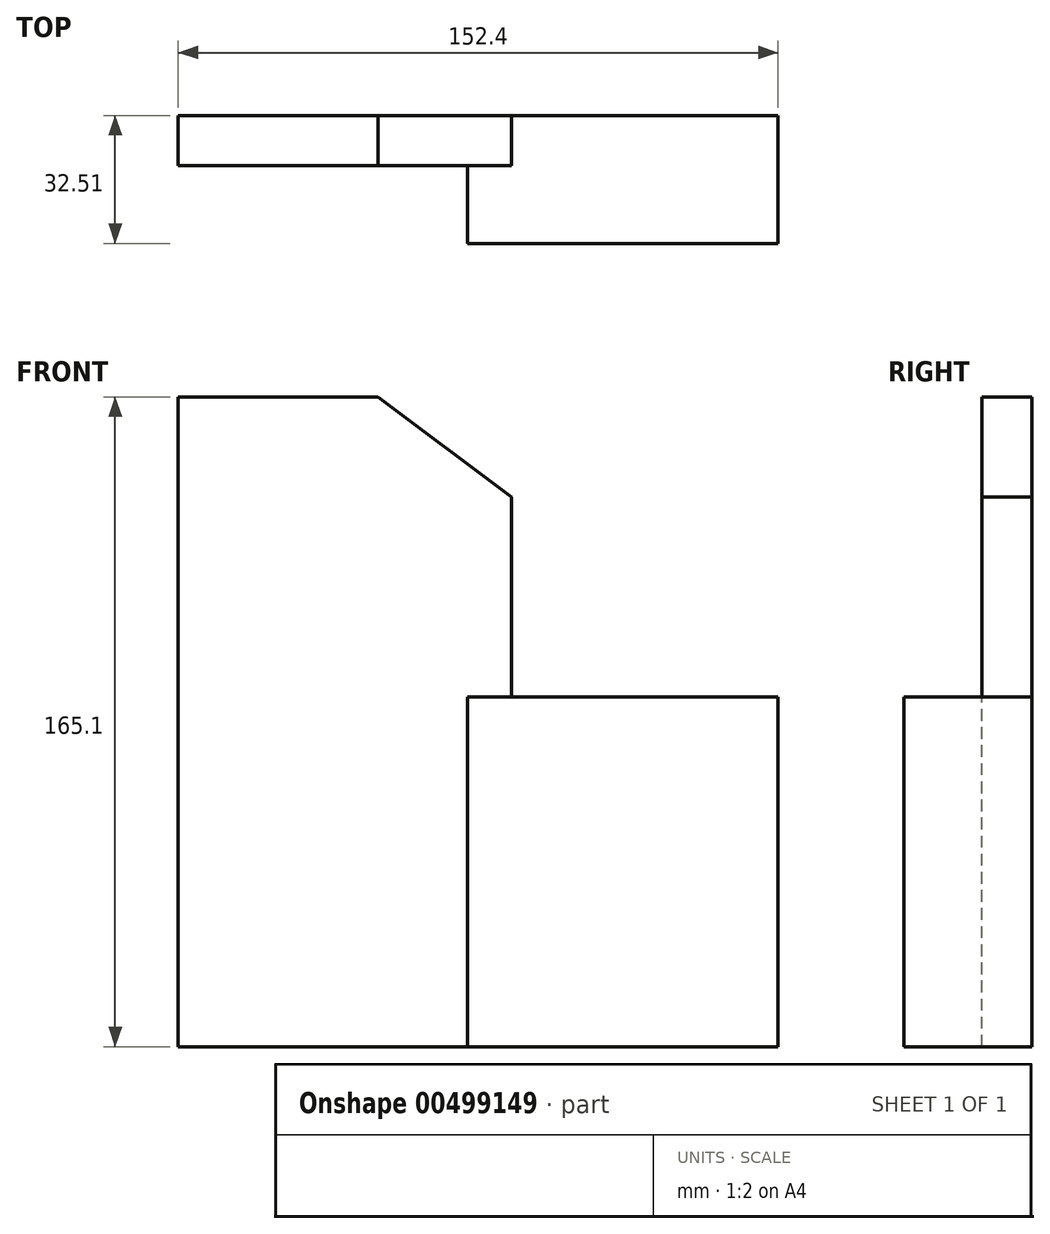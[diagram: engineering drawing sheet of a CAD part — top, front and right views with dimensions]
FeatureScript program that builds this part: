
annotation { "Feature Type Name" : "Feature", "Feature Type Description" : "" }
export const myFeature = defineFeature(function(context is Context, id is Id, definition is map)
    precondition{}
    {
        {
            var Q0;
            Q0=qCreatedBy(makeId("Top.planeOp"),FACE);
            var sketch = newSketch(context, id + "F0", { "sketchPlane" : qUnion([Q0])});
            skLineSegment(sketch, "E0.bottom", {"start": v(76.2, 6.35) * mm, "end": v(-76.2, 6.35) * mm});
            skLineSegment(sketch, "E0.top", {"start": v(76.2, -6.35) * mm, "end": v(-76.2, -6.35) * mm});
            skLineSegment(sketch, "E0.left", {"start": v(76.2, 6.35) * mm, "end": v(76.2, -6.35) * mm});
            skLineSegment(sketch, "E0.right", {"start": v(-76.2, 6.35) * mm, "end": v(-76.2, -6.35) * mm});
            skPoint(sketch, "E0.middle", {"position": v(0, 0) * mm});
            skSolve(sketch);
        }
        {
            var Q0;
            Q0=makeQuery(id+"F0.imprint","IMPRINT",FACE,{"disambiguationData":[TD([[makeQuery(id+"F0.imprint","IMPRINT",EDGE,{"derivedFrom":sQuery(id+"F0.wireOp",EDGE,"E0.bottom")}),1.0]])]});
            extrude(context, id + "F1", {"entities" : qUnion([Q0]), "oppositeDirection" : true, "depth" : 165.1 * mm});
        }
        {
            var Q0;
            Q0=makeQuery(id+"F1.opExtrude","CAP_EDGE",EDGE,{"disambiguationData":[OSD([sQuery(id+"F0.wireOp",EDGE,"E0.left")])],"isStart":true});
            chamfer(context, id + "F2", {"entities" : qUnion([Q0]), "chamferType" : ChamferType.TWO_OFFSETS, "width1" : 76.2 * mm, "oppositeDirection" : false, "width2" : 101.6 * mm, "tangentPropagation" : true});
        }
        {
            var Q0;
            Q0=makeQuery(id+"F1.opExtrude","SWEPT_FACE",FACE,{"disambiguationData":[OSD([sQuery(id+"F0.wireOp",EDGE,"E0.top")])]});
            var sketch = newSketch(context, id + "F3", { "sketchPlane" : qUnion([Q0])});
            skLineSegment(sketch, "E1.bottom", {"start": v(76.2, -165.1) * mm, "end": v(-2.7, -165.1) * mm});
            skLineSegment(sketch, "E2", {"start": v(-75.67, -94.08) * mm, "end": v(-76.2, -94.08) * mm});
            skLineSegment(sketch, "E3", {"start": v(-76.2, 0) * mm, "end": v(-75.67, -94.08) * mm});
            skPoint(sketch, "E4.endSnap0", {"position": v(-34.93, 0) * mm});
            skLineSegment(sketch, "E5", {"start": v(-2.7, -165.1) * mm, "end": v(-2.7, -76.2) * mm});
            skLineSegment(sketch, "E6", {"start": v(76.2, -120.65) * mm, "end": v(76.2, -165.1) * mm});
            skLineSegment(sketch, "E7", {"start": v(-2.7, -165.1) * mm, "end": v(76.2, -165.1) * mm});
            skLineSegment(sketch, "E8", {"start": v(-2.7, -76.2) * mm, "end": v(76.2, -76.2) * mm});
            skLineSegment(sketch, "E9", {"start": v(76.2, -76.2) * mm, "end": v(76.2, -120.65) * mm});
            skSolve(sketch);
        }
        {
            var Q0;
            Q0=makeQuery(id+"F3.imprint","IMPRINT",FACE,{"disambiguationData":[TD([[makeQuery(id+"F3.imprint","IMPRINT",EDGE,{"derivedFrom":sQuery(id+"F3.wireOp",EDGE,"E5")}),-1.0]])]});
            extrude(context, id + "F4", {"entities" : qUnion([Q0]), "operationType" : NewBodyOperationType.ADD, "depth" : 19.8 * mm});
        }
        {
            var Q0;
            Q0=makeQuery(id+"F1.opExtrude","SWEPT_FACE",FACE,{"disambiguationData":[OSD([sQuery(id+"F0.wireOp",EDGE,"E0.bottom")])]});
            var sketch = newSketch(context, id + "F5", { "sketchPlane" : qUnion([Q0])});
            skLineSegment(sketch, "E10", {"start": v(-76.2, -76.2) * mm, "end": v(-8.47, -25.4) * mm});
            skLineSegment(sketch, "E11", {"start": v(-8.47, -25.4) * mm, "end": v(-8.47, -76.2) * mm});
            skLineSegment(sketch, "E12", {"start": v(-8.47, -76.2) * mm, "end": v(-76.2, -76.2) * mm});
            skSolve(sketch);
        }
        {
            var Q0;
            Q0=makeQuery(id+"F5.imprint","IMPRINT",FACE,{"disambiguationData":[TD([[makeQuery(id+"F5.imprint","IMPRINT",EDGE,{"derivedFrom":sQuery(id+"F5.wireOp",EDGE,"E10")}),1.0]])]});
            extrude(context, id + "F6", {"entities" : qUnion([Q0]), "operationType" : NewBodyOperationType.REMOVE, "oppositeDirection" : true, "depth" : 25.4 * mm});
        }
    });
